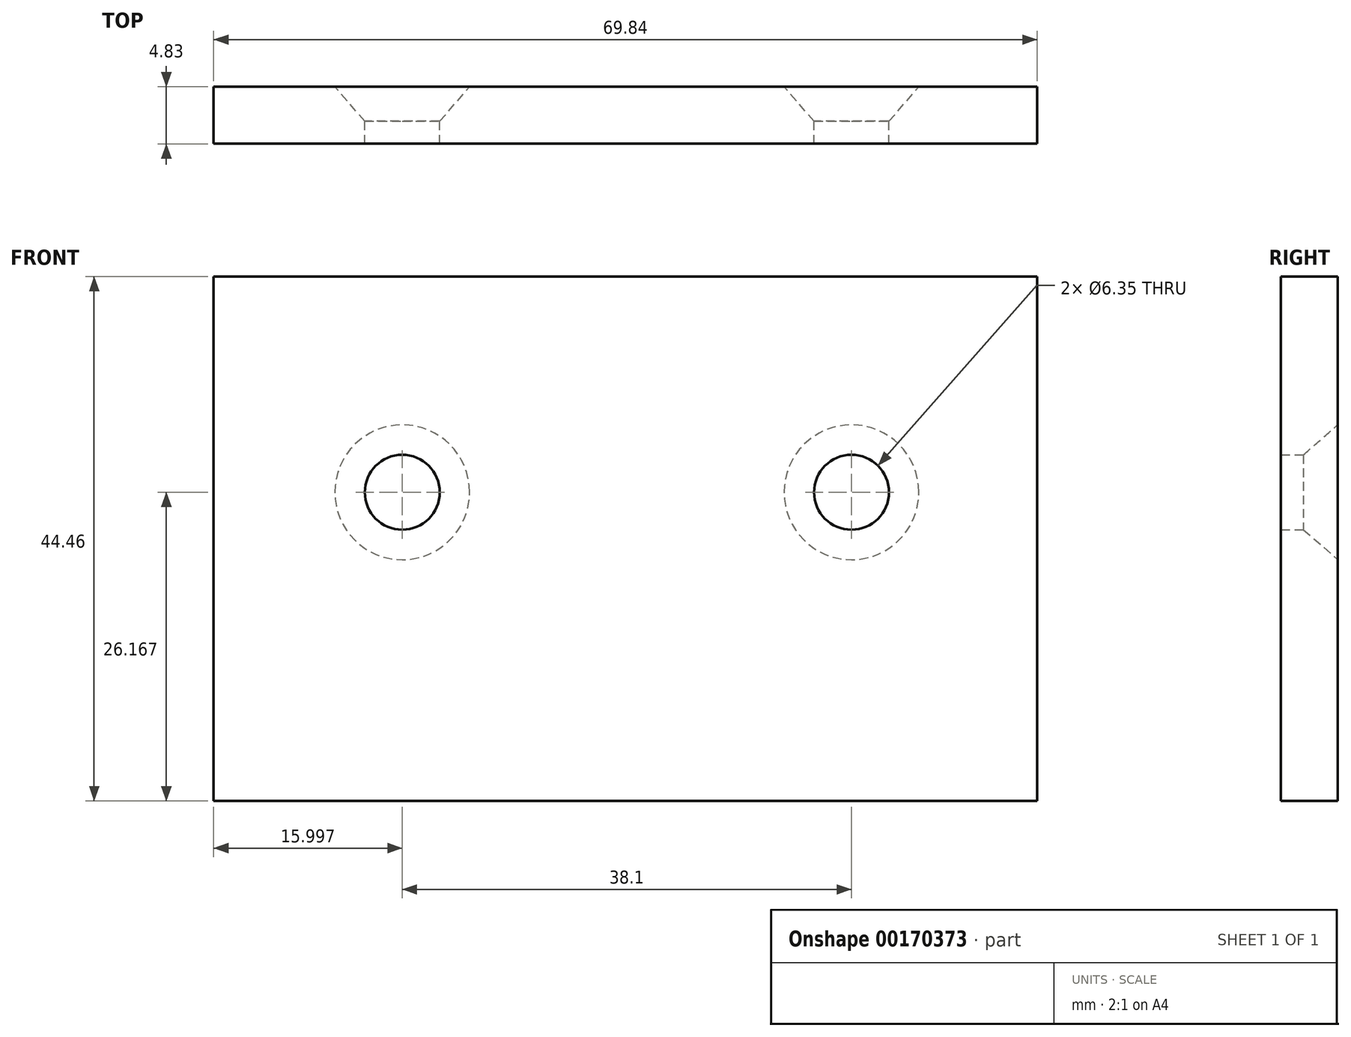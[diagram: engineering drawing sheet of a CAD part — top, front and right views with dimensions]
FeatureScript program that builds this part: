
annotation { "Feature Type Name" : "Feature", "Feature Type Description" : "" }
export const myFeature = defineFeature(function(context is Context, id is Id, definition is map)
    precondition{}
    {
        {
            var Q0;
            Q0=qCreatedBy(makeId("Front.planeOp"),FACE);
            var sketch = newSketch(context, id + "F0", { "sketchPlane" : qUnion([Q0])});
            skLineSegment(sketch, "E0.bottom", {"start": v(-34.92, 22.23) * mm, "end": v(34.93, 22.23) * mm});
            skLineSegment(sketch, "E0.top", {"start": v(-34.92, -22.23) * mm, "end": v(34.92, -22.23) * mm});
            skLineSegment(sketch, "E0.left", {"start": v(-34.92, 22.23) * mm, "end": v(-34.93, -22.22) * mm});
            skLineSegment(sketch, "E0.right", {"start": v(34.93, 22.23) * mm, "end": v(34.92, -22.22) * mm});
            skPoint(sketch, "E0.middle", {"position": v(0, 0) * mm});
            skPoint(sketch, "E1", {"position": v(-18.92, 3.94) * mm});
            skPoint(sketch, "E2", {"position": v(19.18, 3.94) * mm});
            skSolve(sketch);
        }
        {
            var Q0;
            Q0 = qSketchRegion(id + "F0", true);
            extrude(context, id + "F1", {"entities" : qUnion([Q0]), "depth" : 4.83 * mm});
        }
        {
            var Q0;
            Q0=sQuery(id+"F0.wireOp",VERTEX,"E1");
            var Q1;
            Q1=sQuery(id+"F0.wireOp",VERTEX,"E2");
            var Q2;
            Q2=makeQuery(id+"F1.opExtrude","SWEPT_BODY",BODY,{"disambiguationData":[OSD([sQuery(id+"F0.wireOp",EDGE,"E0.bottom"),sQuery(id+"F0.wireOp",EDGE,"E0.top"),sQuery(id+"F0.wireOp",EDGE,"E0.left"),sQuery(id+"F0.wireOp",EDGE,"E0.right")])]});
            hole(context, id + "F2", {"style" : HoleStyle.C_SINK, "endStyle" : HoleEndStyle.THROUGH, "oppositeDirection" : true, "holeDiameter" : 6.35 * mm, "cSinkDiameter" : 11.43 * mm, "cSinkAngle" : 82 * degree, "locations" : qUnion([Q0, Q1]), "scope" : qUnion([Q2]), "isTappedThrough" : true});
        }
    });
